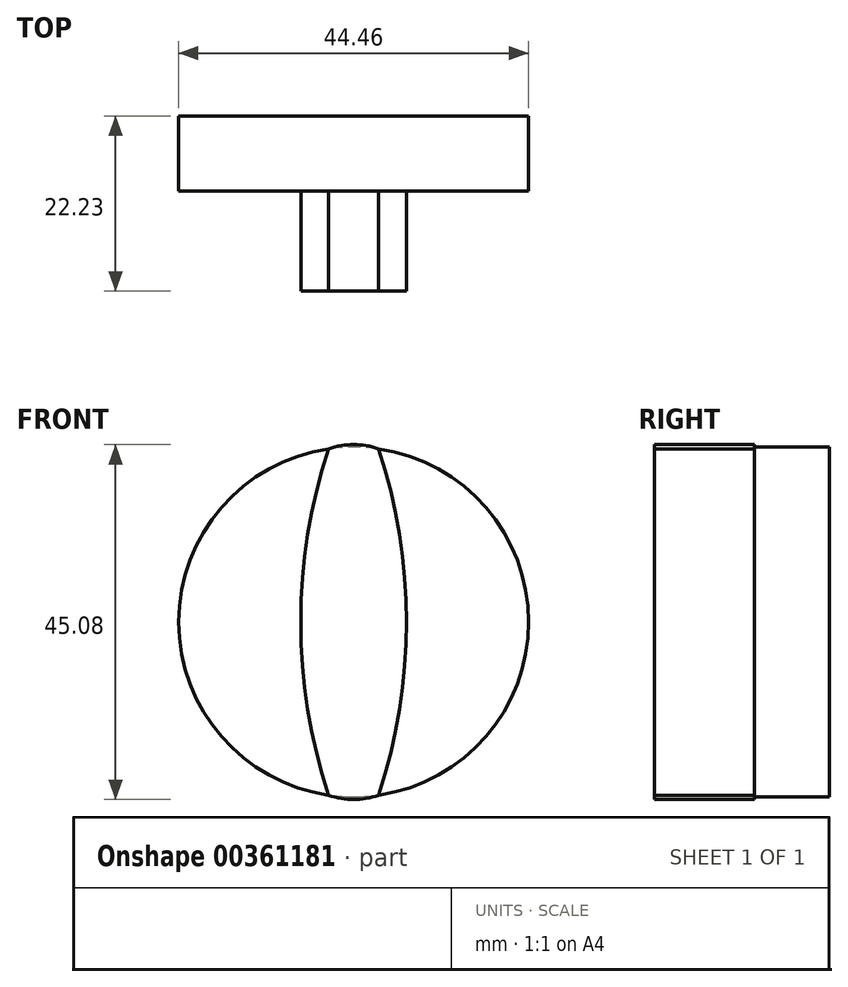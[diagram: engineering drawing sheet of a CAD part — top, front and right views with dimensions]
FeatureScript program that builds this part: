
annotation { "Feature Type Name" : "Feature", "Feature Type Description" : "" }
export const myFeature = defineFeature(function(context is Context, id is Id, definition is map)
    precondition{}
    {
        {
            var Q0;
            Q0=qCreatedBy(makeId("Front.planeOp"),FACE);
            var sketch = newSketch(context, id + "F0", { "sketchPlane" : qUnion([Q0])});
            skCircle(sketch, "E0", {"center": v(0, 0) * mm, "radius": 22.22 * mm});
            skSolve(sketch);
        }
        {
            var Q0;
            Q0=makeQuery(id+"F0.imprint","IMPRINT",FACE,{"disambiguationData":[TD([[makeQuery(id+"F0.imprint","IMPRINT",EDGE,{"derivedFrom":sQuery(id+"F0.wireOp",EDGE,"E0")}),1.0]])]});
            extrude(context, id + "F1", {"entities" : qUnion([Q0]), "depth" : 9.52 * mm});
        }
        {
            var Q0;
            Q0=makeQuery(id+"F1.opExtrude","CAP_FACE",FACE,{"disambiguationData":[OSD([sQuery(id+"F0.wireOp",EDGE,"E0")])],"isStart":false});
            var sketch = newSketch(context, id + "F2", { "sketchPlane" : qUnion([Q0])});
            skArc(sketch, "E1", {"start": v(-3.17, 22) * mm, "mid": v(-6.7, 0) * mm, "end": v(-3.17, -22) * mm});
            skArc(sketch, "E2", {"start": v(3.17, 22) * mm, "mid": v(0, 22.54) * mm, "end": v(-3.17, 22) * mm});
            skPoint(sketch, "E3", {"position": v(0, 22.54) * mm});
            skArc(sketch, "E4.MirrorCS", {"start": v(3.17, 22) * mm, "mid": v(6.7, 0) * mm, "end": v(3.17, -22) * mm});
            skArc(sketch, "E5.MirrorCS", {"start": v(3.17, -22) * mm, "mid": v(0, -22.54) * mm, "end": v(-3.17, -22) * mm});
            skSolve(sketch);
        }
        {
            var Q0;
            Q0 = qSketchRegion(id + "F2", true);
            extrude(context, id + "F3", {"entities" : qUnion([Q0]), "operationType" : NewBodyOperationType.ADD, "depth" : 12.7 * mm});
        }
    });
